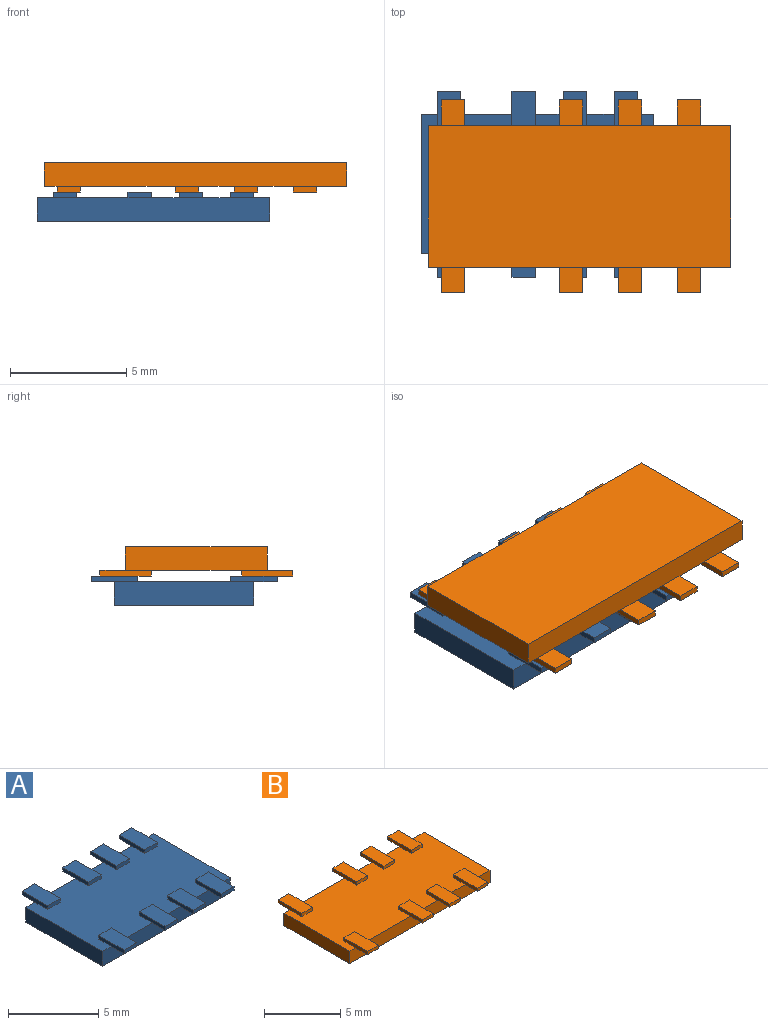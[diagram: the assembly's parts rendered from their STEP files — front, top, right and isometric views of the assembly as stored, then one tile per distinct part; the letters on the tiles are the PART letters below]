
ASSEMBLY  parts=2 mates=1
PART A: 54 faces, bbox 10x8x1.3 mm
  f0: plane 10x6mm, normal (0,0,1), area 52mm2, adj f1,f2,f3,f4,f7,f8,f10,f13
  f1: plane 10x1mm, normal (0,-1,0), area 10mm2, adj f0,f2,f4,f5,f17,f23,f29,f35
  f2: plane 6x1mm, normal (1,0,0), area 6mm2, adj f0,f1,f3,f5
  f3: plane 10x1mm, normal (0,1,0), area 10mm2, adj f0,f2,f4,f5,f6,f36,f42,f48
  f4: plane 6x1mm, normal (-1,0,0), area 6mm2, adj f0,f1,f3,f5
  f5: plane 10x6mm, normal (0,0,-1), area 60mm2, adj f1,f2,f3,f4
  f6: plane 1x1mm, normal (0,0,-1), area 1mm2, adj f3,f8,f9,f10
  f7: plane 1x0.25mm, normal (0,-1,0), area 0.2mm2, adj f0,f8,f10,f11
  f8: plane 2x0.25mm, normal (1,0,0), area 0.5mm2, adj f0,f6,f7,f9,f11
  f9: plane 1x0.25mm, normal (0,1,0), area 0.2mm2, adj f6,f8,f10,f11
  f10: plane 2x0.25mm, normal (-1,0,0), area 0.5mm2, adj f0,f6,f7,f9,f11
  f11: plane 2x1mm, normal (0,0,1), area 2mm2, adj f7,f8,f9,f10
  f12: plane 1x0.25mm, normal (0,-1,0), area 0.2mm2, adj f13,f15,f16,f17
  f13: plane 2x0.25mm, normal (1,0,0), area 0.5mm2, adj f0,f12,f14,f16,f17
  f14: plane 1x0.25mm, normal (0,1,0), area 0.2mm2, adj f0,f13,f15,f16
  f15: plane 2x0.25mm, normal (-1,0,0), area 0.5mm2, adj f0,f12,f14,f16,f17
  f16: plane 2x1mm, normal (0,0,1), area 2mm2, adj f12,f13,f14,f15
  f17: plane 1x1mm, normal (0,0,-1), area 1mm2, adj f1,f12,f13,f15
  f18: plane 1x0.25mm, normal (0,-1,0), area 0.2mm2, adj f19,f21,f22,f23
  f19: plane 2x0.25mm, normal (1,0,0), area 0.5mm2, adj f0,f18,f20,f22,f23
  f20: plane 1x0.25mm, normal (0,1,0), area 0.2mm2, adj f0,f19,f21,f22
  f21: plane 2x0.25mm, normal (-1,0,0), area 0.5mm2, adj f0,f18,f20,f22,f23
  f22: plane 2x1mm, normal (0,0,1), area 2mm2, adj f18,f19,f20,f21
  f23: plane 1x1mm, normal (0,0,-1), area 1mm2, adj f1,f18,f19,f21
  f24: plane 1x0.25mm, normal (0,-1,0), area 0.2mm2, adj f25,f27,f28,f29
  f25: plane 2x0.25mm, normal (1,0,0), area 0.5mm2, adj f0,f24,f26,f28,f29
  f26: plane 1x0.25mm, normal (0,1,0), area 0.2mm2, adj f0,f25,f27,f28
  f27: plane 2x0.25mm, normal (-1,0,0), area 0.5mm2, adj f0,f24,f26,f28,f29
  f28: plane 2x1mm, normal (0,0,1), area 2mm2, adj f24,f25,f26,f27
  f29: plane 1x1mm, normal (0,0,-1), area 1mm2, adj f1,f24,f25,f27
  f30: plane 1x0.25mm, normal (0,-1,0), area 0.2mm2, adj f31,f33,f34,f35
  f31: plane 2x0.25mm, normal (1,0,0), area 0.5mm2, adj f0,f30,f32,f34,f35
  f32: plane 1x0.25mm, normal (0,1,0), area 0.2mm2, adj f0,f31,f33,f34
  f33: plane 2x0.25mm, normal (-1,0,0), area 0.5mm2, adj f0,f30,f32,f34,f35
  f34: plane 2x1mm, normal (0,0,1), area 2mm2, adj f30,f31,f32,f33
  f35: plane 1x1mm, normal (0,0,-1), area 1mm2, adj f1,f30,f31,f33
  f36: plane 1x1mm, normal (0,0,-1), area 1mm2, adj f3,f37,f39,f40
  f37: plane 2x0.25mm, normal (-1,0,0), area 0.5mm2, adj f0,f36,f38,f40,f41
  f38: plane 1x0.25mm, normal (0,-1,0), area 0.2mm2, adj f0,f37,f39,f41
  f39: plane 2x0.25mm, normal (1,0,0), area 0.5mm2, adj f0,f36,f38,f40,f41
  f40: plane 1x0.25mm, normal (0,1,0), area 0.2mm2, adj f36,f37,f39,f41
  f41: plane 2x1mm, normal (0,0,1), area 2mm2, adj f37,f38,f39,f40
  f42: plane 1x1mm, normal (0,0,-1), area 1mm2, adj f3,f43,f45,f46
  f43: plane 2x0.25mm, normal (-1,0,0), area 0.5mm2, adj f0,f42,f44,f46,f47
  f44: plane 1x0.25mm, normal (0,-1,0), area 0.2mm2, adj f0,f43,f45,f47
  f45: plane 2x0.25mm, normal (1,0,0), area 0.5mm2, adj f0,f42,f44,f46,f47
  f46: plane 1x0.25mm, normal (0,1,0), area 0.2mm2, adj f42,f43,f45,f47
  f47: plane 2x1mm, normal (0,0,1), area 2mm2, adj f43,f44,f45,f46
  f48: plane 1x1mm, normal (0,0,-1), area 1mm2, adj f3,f49,f51,f52
  f49: plane 2x0.25mm, normal (-1,0,0), area 0.5mm2, adj f0,f48,f50,f52,f53
  f50: plane 1x0.25mm, normal (0,-1,0), area 0.2mm2, adj f0,f49,f51,f53
  f51: plane 2x0.25mm, normal (1,0,0), area 0.5mm2, adj f0,f48,f50,f52,f53
  f52: plane 1x0.25mm, normal (0,1,0), area 0.2mm2, adj f48,f49,f51,f53
  f53: plane 2x1mm, normal (0,0,1), area 2mm2, adj f49,f50,f51,f52
PART B: 54 faces, bbox 13x8.3x1.3 mm
  f0: plane 13x6.1mm, normal (0,0,1), area 70.5mm2, adj f1,f2,f3,f4,f6,f7,f9,f13
  f1: plane 13x1mm, normal (0,-1,0), area 13mm2, adj f0,f2,f4,f5,f11,f41,f47,f53
  f2: plane 6.1x1mm, normal (1,0,0), area 6.1mm2, adj f0,f1,f3,f5
  f3: plane 13x1mm, normal (0,1,0), area 13mm2, adj f0,f2,f4,f5,f12,f18,f24,f30
  f4: plane 6.1x1mm, normal (-1,0,0), area 6.1mm2, adj f0,f1,f3,f5
  f5: plane 13x6.1mm, normal (0,0,-1), area 79.3mm2, adj f1,f2,f3,f4
  f6: plane 1x0.25mm, normal (0,1,0), area 0.2mm2, adj f0,f7,f9,f10
  f7: plane 2.2x0.25mm, normal (-1,0,0), area 0.6mm2, adj f0,f6,f8,f10,f11
  f8: plane 1x0.25mm, normal (0,-1,0), area 0.2mm2, adj f7,f9,f10,f11
  f9: plane 2.2x0.25mm, normal (1,0,0), area 0.6mm2, adj f0,f6,f8,f10,f11
  f10: plane 2.2x1mm, normal (0,0,1), area 2.2mm2, adj f6,f7,f8,f9
  f11: plane 1.1x1mm, normal (0,0,-1), area 1.1mm2, adj f1,f7,f8,f9
  f12: plane 1.1x1mm, normal (0,0,-1), area 1.1mm2, adj f3,f13,f15,f16
  f13: plane 2.2x0.25mm, normal (-1,0,0), area 0.6mm2, adj f0,f12,f14,f16,f17
  f14: plane 1x0.25mm, normal (0,-1,0), area 0.2mm2, adj f0,f13,f15,f17
  f15: plane 2.2x0.25mm, normal (1,0,0), area 0.6mm2, adj f0,f12,f14,f16,f17
  f16: plane 1x0.25mm, normal (0,1,0), area 0.2mm2, adj f12,f13,f15,f17
  f17: plane 2.2x1mm, normal (0,0,1), area 2.2mm2, adj f13,f14,f15,f16
  f18: plane 1.1x1mm, normal (0,0,-1), area 1.1mm2, adj f3,f19,f21,f22
  f19: plane 2.2x0.25mm, normal (-1,0,0), area 0.6mm2, adj f0,f18,f20,f22,f23
  f20: plane 1x0.25mm, normal (0,-1,0), area 0.2mm2, adj f0,f19,f21,f23
  f21: plane 2.2x0.25mm, normal (1,0,0), area 0.6mm2, adj f0,f18,f20,f22,f23
  f22: plane 1x0.25mm, normal (0,1,0), area 0.2mm2, adj f18,f19,f21,f23
  f23: plane 2.2x1mm, normal (0,0,1), area 2.2mm2, adj f19,f20,f21,f22
  f24: plane 1.1x1mm, normal (0,0,-1), area 1.1mm2, adj f3,f25,f27,f28
  f25: plane 2.2x0.25mm, normal (-1,0,0), area 0.6mm2, adj f0,f24,f26,f28,f29
  f26: plane 1x0.25mm, normal (0,-1,0), area 0.2mm2, adj f0,f25,f27,f29
  f27: plane 2.2x0.25mm, normal (1,0,0), area 0.6mm2, adj f0,f24,f26,f28,f29
  f28: plane 1x0.25mm, normal (0,1,0), area 0.2mm2, adj f24,f25,f27,f29
  f29: plane 2.2x1mm, normal (0,0,1), area 2.2mm2, adj f25,f26,f27,f28
  f30: plane 1.1x1mm, normal (0,0,-1), area 1.1mm2, adj f3,f31,f33,f34
  f31: plane 2.2x0.25mm, normal (-1,0,0), area 0.6mm2, adj f0,f30,f32,f34,f35
  f32: plane 1x0.25mm, normal (0,-1,0), area 0.2mm2, adj f0,f31,f33,f35
  f33: plane 2.2x0.25mm, normal (1,0,0), area 0.6mm2, adj f0,f30,f32,f34,f35
  f34: plane 1x0.25mm, normal (0,1,0), area 0.2mm2, adj f30,f31,f33,f35
  f35: plane 2.2x1mm, normal (0,0,1), area 2.2mm2, adj f31,f32,f33,f34
  f36: plane 1x0.25mm, normal (0,-1,0), area 0.2mm2, adj f37,f39,f40,f41
  f37: plane 2.2x0.25mm, normal (1,0,0), area 0.6mm2, adj f0,f36,f38,f40,f41
  f38: plane 1x0.25mm, normal (0,1,0), area 0.2mm2, adj f0,f37,f39,f40
  f39: plane 2.2x0.25mm, normal (-1,0,0), area 0.6mm2, adj f0,f36,f38,f40,f41
  f40: plane 2.2x1mm, normal (0,0,1), area 2.2mm2, adj f36,f37,f38,f39
  f41: plane 1.1x1mm, normal (0,0,-1), area 1.1mm2, adj f1,f36,f37,f39
  f42: plane 1x0.25mm, normal (0,-1,0), area 0.2mm2, adj f43,f45,f46,f47
  f43: plane 2.2x0.25mm, normal (1,0,0), area 0.6mm2, adj f0,f42,f44,f46,f47
  f44: plane 1x0.25mm, normal (0,1,0), area 0.2mm2, adj f0,f43,f45,f46
  f45: plane 2.2x0.25mm, normal (-1,0,0), area 0.6mm2, adj f0,f42,f44,f46,f47
  f46: plane 2.2x1mm, normal (0,0,1), area 2.2mm2, adj f42,f43,f44,f45
  f47: plane 1.1x1mm, normal (0,0,-1), area 1.1mm2, adj f1,f42,f43,f45
  f48: plane 1x0.25mm, normal (0,-1,0), area 0.2mm2, adj f49,f51,f52,f53
  f49: plane 2.2x0.25mm, normal (1,0,0), area 0.6mm2, adj f0,f48,f50,f52,f53
  f50: plane 1x0.25mm, normal (0,1,0), area 0.2mm2, adj f0,f49,f51,f52
  f51: plane 2.2x0.25mm, normal (-1,0,0), area 0.6mm2, adj f0,f48,f50,f52,f53
  f52: plane 2.2x1mm, normal (0,0,1), area 2.2mm2, adj f48,f49,f50,f51
  f53: plane 1.1x1mm, normal (0,0,-1), area 1.1mm2, adj f1,f48,f49,f51
PLACE A t=(-0.87,0.47,3.92)mm
PLACE B rot(axis=(1,0,0),180deg) t=(0.93,-0.05,6.42)mm
MATE planar B.f10 <-> A.f16  axis (0,0,-1) through (-4.52,3,5.17)mm
